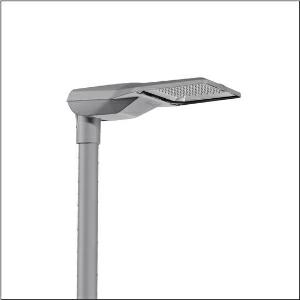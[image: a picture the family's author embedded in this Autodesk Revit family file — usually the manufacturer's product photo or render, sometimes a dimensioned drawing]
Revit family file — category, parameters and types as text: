
# Revit family: streetlight_sl_21_iq_midi___pl52_5xe3h31d08mb_2c0b
name_source: partatom
category: Lighting Fixtures
units: mm (PartAtom-declared; Revit-internal decimal feet)

## family parameters
Cut with Voids When Loaded = No
Host = Face
Light Source = No
Part Type = Normal
Room Calculation Point = No
Round Connector Dimension = Use Diameter
Shared = No

## types (1)
- --- (1 x LED, 19170 lm, 146.7 W, 3000K)
    Apparent Load = 147 VA
    CIE Flux Codes = 27 59 98 100 100
    Color Rendering = 70
    Color Temperature = 3000K
    Default Elevation = 1800 mm
    Description = Streetlight SL 21 iQ midi, mast luminaire, primary light control with lens, of PMMA, primary optical cover: cover, of toughened safety glass, transparent, light distribution: PL52, light emission: direct distribution, primary light characteristic: asymmetric, installation type: post-top, side-entry, LED, High Power LED, rated luminous flux: 19.170lm, luminous efficacy: 131lm/W, light colour: 730, colour temperature: 3000K, control: Auto-Match, Temp-Guard, Lumen-Switch, Night-Set, Smart-Wire, Light-Fading, Desk-Remote (wireless, voltage-free reading and setting of iQ features in the workshop via application-optimized NFC function/RFID function), optimised constant luminous flux control (CLO 2.0), presetting dimming linear, mains connection: 230..240V, AC, 50/60Hz, start of lifetime: 147W, end of service life: 161W, reduction: 62W, luminaire housing, of diecast aluminium, powder-coated, Siteco® metallic grey (DB 702S), corrosivity category C5 mid according to DIN EN ISO 12944, please order mast flange separately, inclination adjustable: 0°, 5°, 10°, 15°, sealing non-destructively replaceable, multi-level sealing system, length: 644mm, width: 335mm, height: 110mm, mast flange for spigot size: 42mm (side-entry): 5XC10008XM4, 60/48mm (side-entry/post-top): 5XC10108XM2, 76/60mm (side-entry/post-top): 5XC10108XM1, protection rating (complete): IP66, insulation class (complete): insulation class II (safety insulation), certification: CE, ENEC, ENEC+, VDE, impact resistance: IK09, permissible operating ambient temperature for outdoor applications: -40..+50°C, standard-compliant lighting for roads and squares, packaging unit: 1 piece

Light Distribution: PL52
    Height = 111 mm
    Lamp = 1 x LED
    Lamp Light Flux = 19170 lm
    Lamp Power = 146.7 W
    Lamp count = 1
    Length = 644 mm
    Luminous efficacy = 131 lm/W
    Manufacturer = Siteco
    ModVariant = No
    Model = 5XE3H31D08MB
    Number of Poles = 1
    OnlyDefault = Yes
    Power Factor = 1
    Product Name = Streetlight SL 21 iQ midi | PL52
    Product group = mast luminaire | pylon top
    ProductGroupID = 6100
    Protection Class = Protection class II
    Protection Degree = IP 66
    RLX_Detail_Level = 1
    RLX_Emergency_Light_Flux = 0 lm
    RLX_Emergency_Type = 0
    RLX_Emergency_Type_DB = No
    RlxData = <blob elided: 100497 chars, md5=81e2c0be>
    Socket = socket
    Standby Power = 0 W
    System Light Flux = 19169 lm
    System Power = 147 W
    Type Comments = factory setting: luminous flux: 100 % | dim-lin: 254 | 753 mA
    Type Image = l_1004298.jpg
    URL = http://relux.com
    VarID = @adj_124961
    Voltage = 0 V
    Weight = 0.00 kg
    Width = 336 mm

## geometry (parser evidence)
native form markers: Blend x4, Sweep x10
no freeform markers — native parametric forms only
